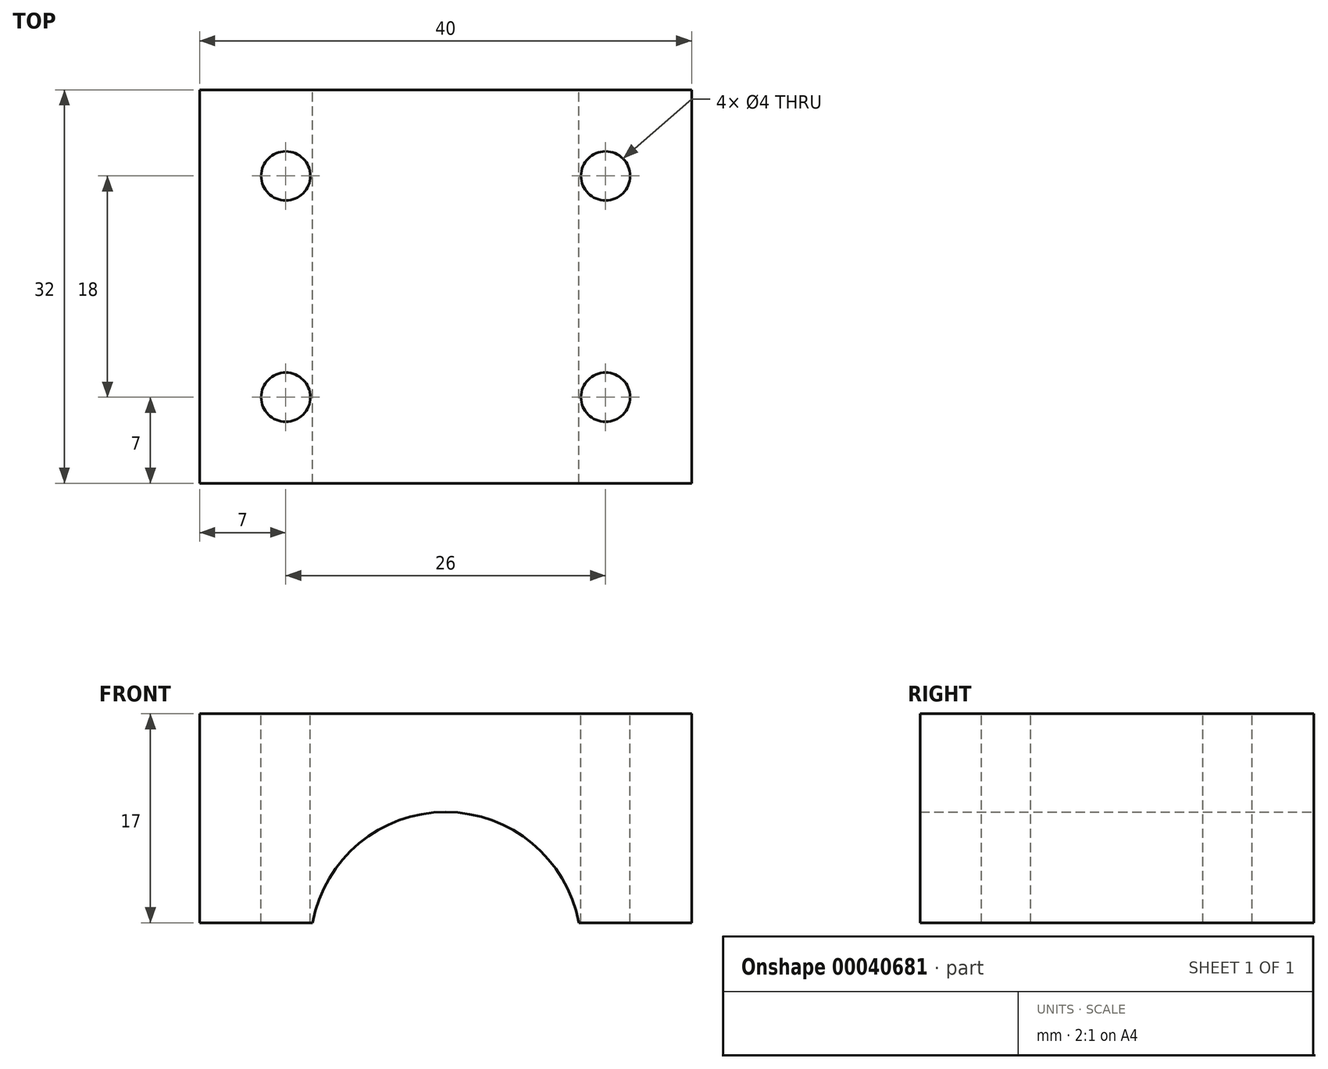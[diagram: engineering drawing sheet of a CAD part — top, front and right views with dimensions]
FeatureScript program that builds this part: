
annotation { "Feature Type Name" : "Feature", "Feature Type Description" : "" }
export const myFeature = defineFeature(function(context is Context, id is Id, definition is map)
    precondition{}
    {
        {
            var Q0;
            Q0=qCreatedBy(makeId("Front.planeOp"),FACE);
            var sketch = newSketch(context, id + "F0", { "sketchPlane" : qUnion([Q0])});
            skArc(sketch, "E0", {"start": v(10.82, 0) * mm, "mid": v(0, 9) * mm, "end": v(-10.82, 0) * mm});
            skLineSegment(sketch, "E1", {"start": v(-10.82, 0) * mm, "end": v(-20, 0) * mm});
            skLineSegment(sketch, "E2", {"start": v(-20, 0) * mm, "end": v(-20, 17) * mm});
            skLineSegment(sketch, "E3", {"start": v(-20, 17) * mm, "end": v(20, 17) * mm});
            skLineSegment(sketch, "E4", {"start": v(20, 17) * mm, "end": v(20, 0) * mm});
            skLineSegment(sketch, "E5", {"start": v(20, 0) * mm, "end": v(10.82, 0) * mm});
            skSolve(sketch);
        }
        {
            var Q0;
            Q0=makeQuery(id+"F0.imprint","IMPRINT",FACE,{"disambiguationData":[TD([[makeQuery(id+"F0.imprint","IMPRINT",EDGE,{"derivedFrom":sQuery(id+"F0.wireOp",EDGE,"E0")}),-1.0]])]});
            extrude(context, id + "F1", {"entities" : qUnion([Q0]), "depth" : 16 * mm});
        }
        {
            var Q0;
            Q0=makeQuery(id+"F1.opExtrude","SWEPT_FACE",FACE,{"disambiguationData":[OSD([sQuery(id+"F0.wireOp",EDGE,"E3")])]});
            var sketch = newSketch(context, id + "F2", { "sketchPlane" : qUnion([Q0])});
            skCircle(sketch, "E6", {"center": v(13, -9) * mm, "radius": 2.21 * mm});
            skCircle(sketch, "E7", {"center": v(-13, -9) * mm, "radius": 2.21 * mm});
            skSolve(sketch);
        }
        {
            var Q0;
            Q0=sQuery(id+"F2.wireOp",VERTEX,"E6.center");
            var Q1;
            Q1=sQuery(id+"F2.wireOp",VERTEX,"E7.center");
            var Q2;
            Q2=makeQuery(id+"F1.opExtrude","SWEPT_BODY",BODY,{"disambiguationData":[OSD([sQuery(id+"F0.wireOp",EDGE,"E0"),sQuery(id+"F0.wireOp",EDGE,"E1"),sQuery(id+"F0.wireOp",EDGE,"E2"),sQuery(id+"F0.wireOp",EDGE,"E3"),sQuery(id+"F0.wireOp",EDGE,"E4"),sQuery(id+"F0.wireOp",EDGE,"E5")])]});
            hole(context, id + "F3", {"style" : HoleStyle.SIMPLE, "holeDiameter" : 4 * mm, "endStyle" : HoleEndStyle.THROUGH, "locations" : qUnion([Q0, Q1]), "scope" : qUnion([Q2])});
        }
        {
            var Q0;
            Q0=makeQuery(id+"F1.opExtrude","SWEPT_FACE",FACE,{"disambiguationData":[OSD([sQuery(id+"F0.wireOp",EDGE,"E3")])]});
            var sketch = newSketch(context, id + "F4", { "sketchPlane" : qUnion([Q0])});
            skCircle(sketch, "E8", {"center": v(-13, -9) * mm, "radius": 5 * mm});
            skCircle(sketch, "E9", {"center": v(13, -9) * mm, "radius": 5 * mm});
            skSolve(sketch);
        }
        {
            var Q0;
            Q0=sQuery(id+"F4.wireOp",EDGE,"E8");
            var Q1;
            Q1=sQuery(id+"F4.wireOp",EDGE,"E9");
            extrude(context, id + "F5", {"bodyType" : ToolBodyType.SURFACE, "surfaceEntities" : qUnion([Q0, Q1]), "oppositeDirection" : true, "depth" : 4 * mm});
        }
        {
            var Q0;
            Q0=makeQuery(id+"F1.opExtrude","SWEPT_BODY",BODY,{"disambiguationData":[OSD([sQuery(id+"F0.wireOp",EDGE,"E0"),sQuery(id+"F0.wireOp",EDGE,"E1"),sQuery(id+"F0.wireOp",EDGE,"E2"),sQuery(id+"F0.wireOp",EDGE,"E3"),sQuery(id+"F0.wireOp",EDGE,"E4"),sQuery(id+"F0.wireOp",EDGE,"E5")])]});
            var Q1;
            Q1=makeQuery(id+"F5.opExtrude","SWEPT_BODY",BODY,{"disambiguationData":[OSD([sQuery(id+"F4.wireOp",EDGE,"E9")])]});
            var Q2;
            Q2=makeQuery(id+"F5.opExtrude","SWEPT_BODY",BODY,{"disambiguationData":[OSD([sQuery(id+"F4.wireOp",EDGE,"E8")])]});
            var Q3;
            Q3=qCreatedBy(makeId("Front.planeOp"),FACE);
            mirror(context, id + "F6", {"operationType" : NewBodyOperationType.ADD, "entities" : qUnion([Q0, Q1, Q2]), "mirrorPlane" : qUnion([Q3])});
        }
    });
